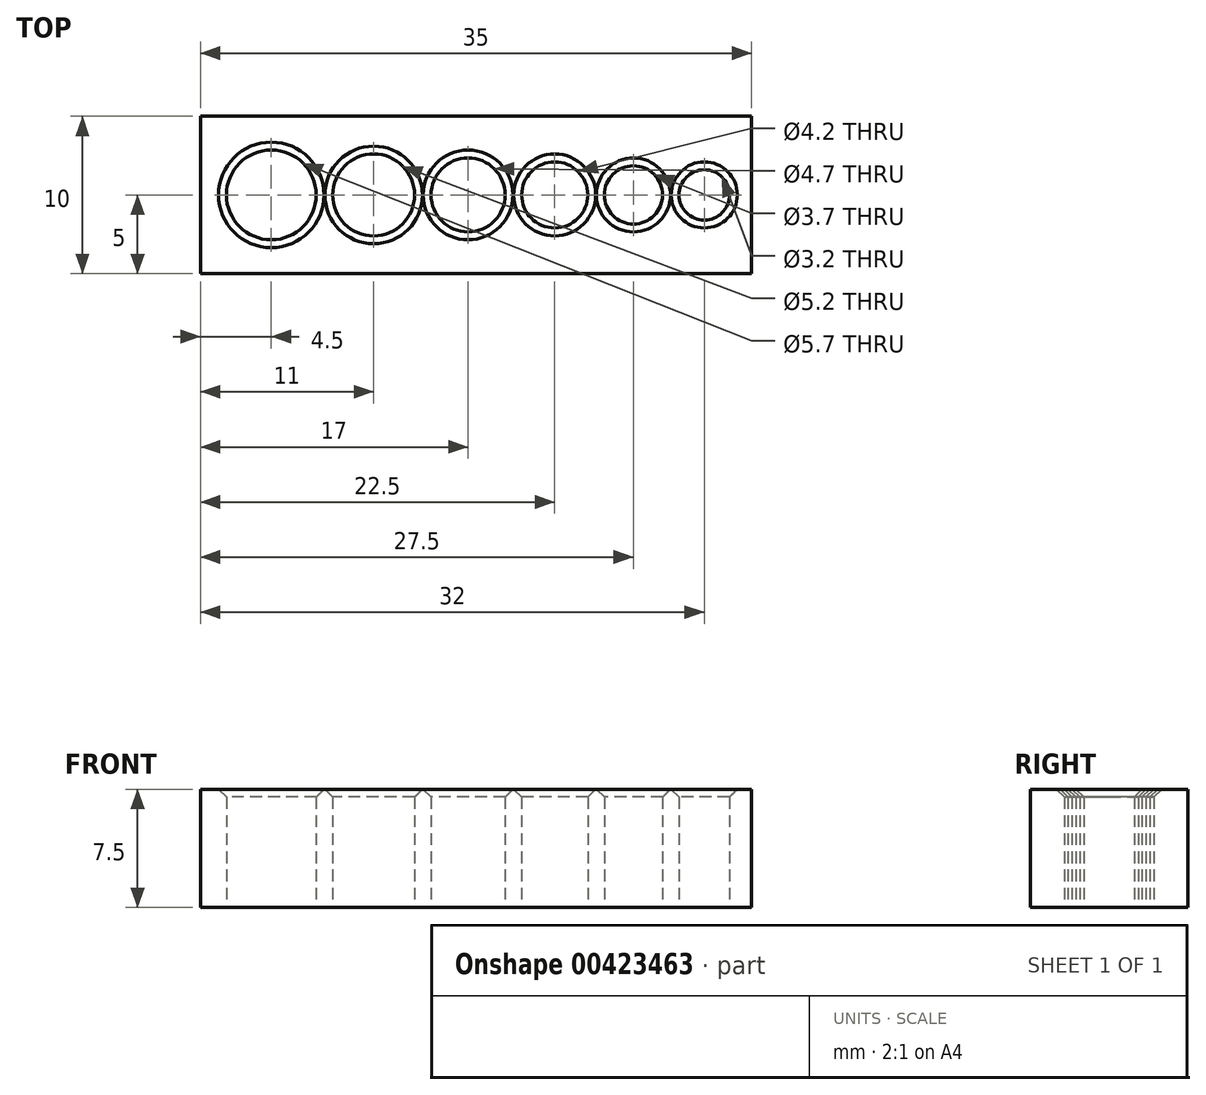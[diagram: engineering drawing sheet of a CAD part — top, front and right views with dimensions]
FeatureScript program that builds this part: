
annotation { "Feature Type Name" : "Feature", "Feature Type Description" : "" }
export const myFeature = defineFeature(function(context is Context, id is Id, definition is map)
    precondition{}
    {
        {
            var Q0;
            Q0=qCreatedBy(makeId("Top.planeOp"),FACE);
            var sketch = newSketch(context, id + "F0", { "sketchPlane" : qUnion([Q0])});
            skLineSegment(sketch, "E0.bottom", {"start": v(12.5, -5) * mm, "end": v(-22.5, -5) * mm});
            skLineSegment(sketch, "E0.top", {"start": v(12.5, 5) * mm, "end": v(-22.5, 5) * mm});
            skLineSegment(sketch, "E0.left", {"start": v(12.5, -5) * mm, "end": v(12.5, 5) * mm});
            skLineSegment(sketch, "E0.right", {"start": v(-22.5, -5) * mm, "end": v(-22.5, 5) * mm});
            skPoint(sketch, "E0.middle", {"position": v(0, 0) * mm});
            skLineSegment(sketch, "E1", {"start": v(-20.74, 0) * mm, "end": v(21.4, 0) * mm, "construction": true});
            skLineSegment(sketch, "E2", {"start": v(0, 13.05) * mm, "end": v(0, -15.4) * mm, "construction": true});
            skCircle(sketch, "E3", {"center": v(0, 0) * mm, "radius": 2.1 * mm});
            skCircle(sketch, "E4", {"center": v(-5.5, 0) * mm, "radius": 2.35 * mm});
            skCircle(sketch, "E5", {"center": v(5, 0) * mm, "radius": 1.85 * mm});
            skCircle(sketch, "E6", {"center": v(9.5, 0) * mm, "radius": 1.6 * mm});
            skCircle(sketch, "E7", {"center": v(-11.5, 0) * mm, "radius": 2.6 * mm});
            skCircle(sketch, "E8", {"center": v(-18, 0) * mm, "radius": 2.85 * mm});
            skPoint(sketch, "E9", {"position": v(12.5, 0) * mm});
            skSolve(sketch);
        }
        {
            var Q0;
            Q0 = qSketchRegion(id + "F0", true);
            extrude(context, id + "F1", {"entities" : qUnion([Q0]), "depth" : 7.5 * mm, "offsetDistance" : 25 * mm});
        }
        {
            var Q0;
            Q0=makeQuery(id+"F1.opExtrude","CAP_EDGE",EDGE,{"disambiguationData":[OSD([sQuery(id+"F0.wireOp",EDGE,"E4")])],"isStart":false});
            var Q1;
            Q1=makeQuery(id+"F1.opExtrude","CAP_EDGE",EDGE,{"disambiguationData":[OSD([sQuery(id+"F0.wireOp",EDGE,"E3")])],"isStart":false});
            var Q2;
            Q2=makeQuery(id+"F1.opExtrude","CAP_EDGE",EDGE,{"disambiguationData":[OSD([sQuery(id+"F0.wireOp",EDGE,"E5")])],"isStart":false});
            var Q3;
            Q3=makeQuery(id+"F1.opExtrude","CAP_EDGE",EDGE,{"disambiguationData":[OSD([sQuery(id+"F0.wireOp",EDGE,"E7")])],"isStart":false});
            var Q4;
            Q4=makeQuery(id+"F1.opExtrude","CAP_EDGE",EDGE,{"disambiguationData":[OSD([sQuery(id+"F0.wireOp",EDGE,"E8")])],"isStart":false});
            var Q5;
            Q5=makeQuery(id+"F1.opExtrude","CAP_EDGE",EDGE,{"disambiguationData":[OSD([sQuery(id+"F0.wireOp",EDGE,"E6")])],"isStart":false});
            chamfer(context, id + "F2", {"entities" : qUnion([Q0, Q1, Q2, Q3, Q4, Q5]), "width" : 0.5 * mm, "tangentPropagation" : true});
        }
    });
